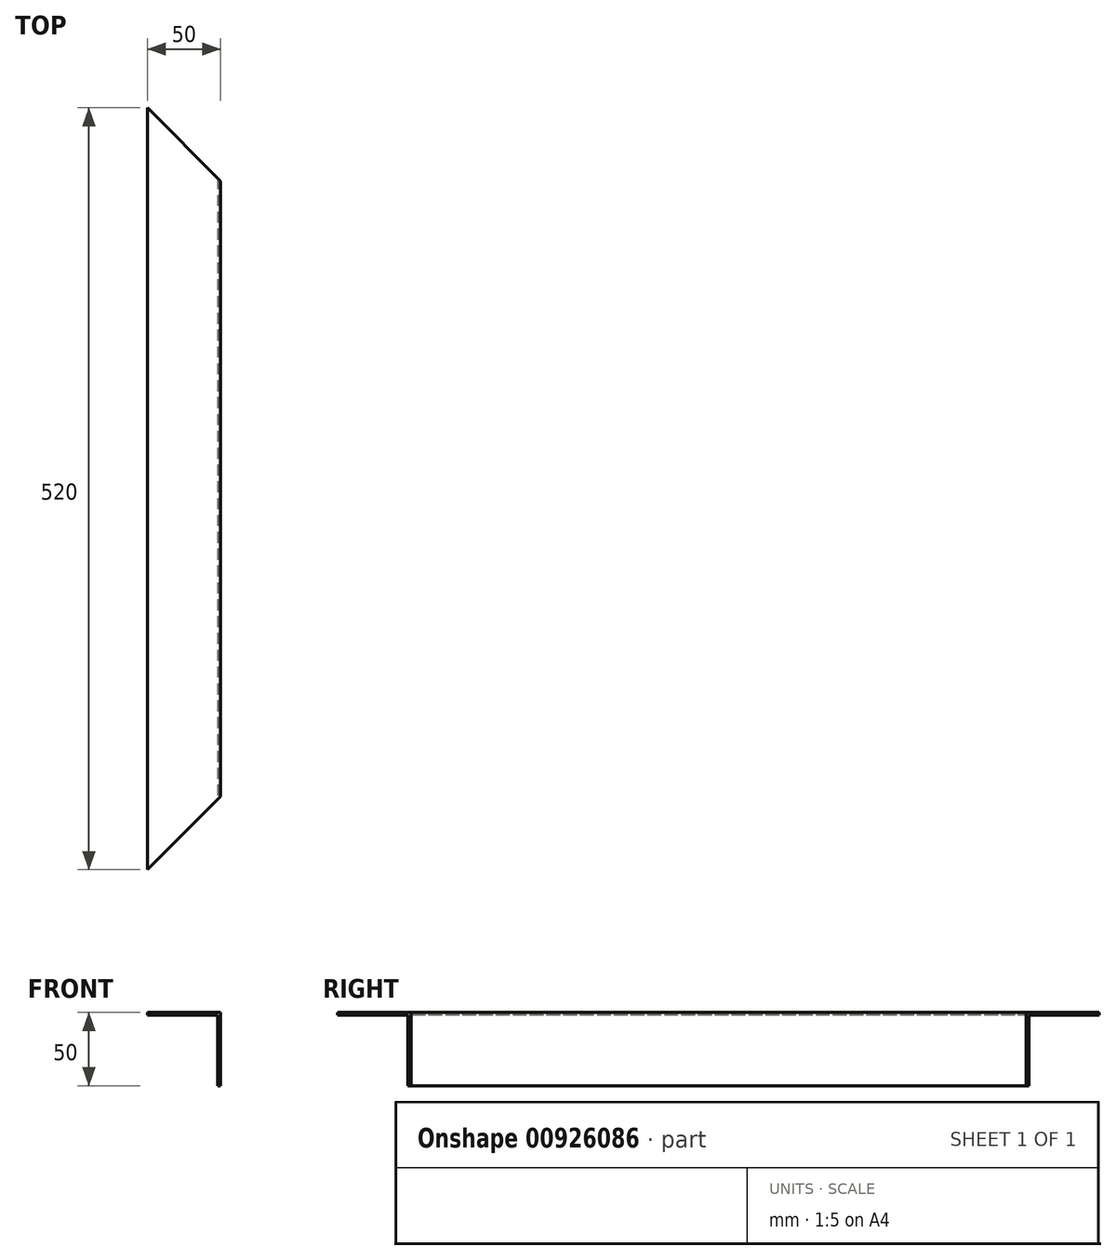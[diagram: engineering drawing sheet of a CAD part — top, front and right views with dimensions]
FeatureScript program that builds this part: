
annotation { "Feature Type Name" : "Feature", "Feature Type Description" : "" }
export const myFeature = defineFeature(function(context is Context, id is Id, definition is map)
    precondition{}
    {
        {
            var Q0;
            Q0=qCreatedBy(makeId("Front.planeOp"),FACE);
            var sketch = newSketch(context, id + "F0", { "sketchPlane" : qUnion([Q0])});
            skLineSegment(sketch, "E0", {"start": v(0, 0) * mm, "end": v(50, 0) * mm});
            skLineSegment(sketch, "E1", {"start": v(50, 0) * mm, "end": v(50, -50) * mm});
            skLineSegment(sketch, "E2.0", {"start": v(48, -2) * mm, "end": v(48, -50) * mm});
            skLineSegment(sketch, "E2.1", {"start": v(0, -2) * mm, "end": v(48, -2) * mm});
            skLineSegment(sketch, "E3", {"start": v(0, -2) * mm, "end": v(0, 0) * mm});
            skLineSegment(sketch, "E4", {"start": v(50, -50) * mm, "end": v(48, -50) * mm});
            skSolve(sketch);
        }
        {
            var Q0;
            Q0 = qSketchRegion(id + "F0", true);
            extrude(context, id + "F1", {"entities" : qUnion([Q0]), "oppositeDirection" : true, "depth" : 520 * mm, "offsetDistance" : 25 * mm});
        }
        {
            var Q0;
            Q0=makeQuery(id+"F1.opExtrude","SWEPT_FACE",FACE,{"disambiguationData":[OSD([sQuery(id+"F0.wireOp",EDGE,"E0")])]});
            var sketch = newSketch(context, id + "F2", { "sketchPlane" : qUnion([Q0])});
            skLineSegment(sketch, "E5", {"start": v(0, 0) * mm, "end": v(50, 0) * mm});
            skLineSegment(sketch, "E6", {"start": v(50, 0) * mm, "end": v(50, 50) * mm});
            skLineSegment(sketch, "E7", {"start": v(50, 50) * mm, "end": v(0, 0) * mm});
            skLineSegment(sketch, "E8", {"start": v(0, 520) * mm, "end": v(50, 520) * mm});
            skLineSegment(sketch, "E9", {"start": v(50, 520) * mm, "end": v(50, 470) * mm});
            skLineSegment(sketch, "E10", {"start": v(50, 470) * mm, "end": v(0, 520) * mm});
            skSolve(sketch);
        }
        {
            var Q0;
            Q0 = qSketchRegion(id + "F2", true);
            extrude(context, id + "F3", {"entities" : qUnion([Q0]), "operationType" : NewBodyOperationType.REMOVE, "endBound" : BoundingType.THROUGH_ALL, "oppositeDirection" : true, "depth" : 25 * mm, "offsetDistance" : 25 * mm});
        }
    });
